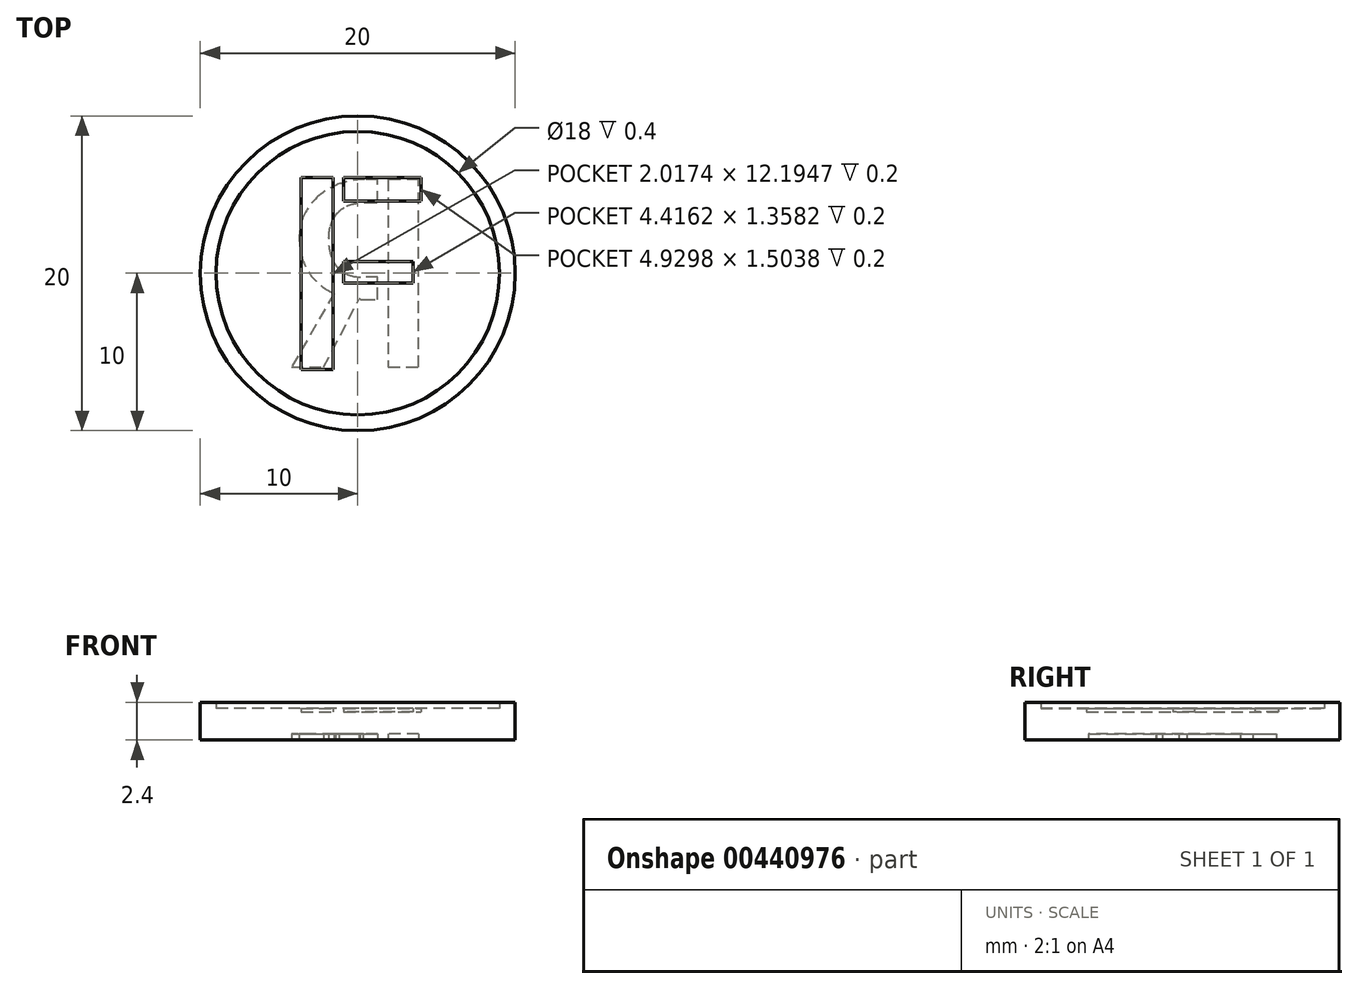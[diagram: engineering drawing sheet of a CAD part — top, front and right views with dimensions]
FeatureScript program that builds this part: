
annotation { "Feature Type Name" : "Feature", "Feature Type Description" : "" }
export const myFeature = defineFeature(function(context is Context, id is Id, definition is map)
    precondition{}
    {
        {
            var Q0;
            Q0=qCreatedBy(makeId("Top.planeOp"),FACE);
            var sketch = newSketch(context, id + "F0", { "sketchPlane" : qUnion([Q0])});
            skCircle(sketch, "E0", {"center": v(0, 0) * mm, "radius": 10 * mm});
            skText(sketch, "E1", { "text": "F", "fontName": "AllertaStencil-Regular.ttf"});
            const initialGuessF0  = {"E1": [-0.00517, -0.0061, 1, 0, 0.0122]};
            skSetInitialGuess(sketch, initialGuessF0);
            skSolve(sketch);
        }
        {
            var Q0;
            Q0=qSketchRegion(id+"F0",true);
            extrude(context, id + "F1", {"entities" : qUnion([Q0]), "depth" : 2 * mm});
        }
        {
            var Q0;
            Q0=makeQuery(id+"F0.imprint","IMPRINT",FACE,{"disambiguationData":[TD([[makeQuery(id+"F0.imprint","IMPRINT",EDGE,{"derivedFrom":sQuery(id+"F0.wireOp",EDGE,"E1.sketch_text.stroke-0")}),-1.0]])]});
            var Q1;
            Q1=makeQuery(id+"F0.imprint","IMPRINT",FACE,{"disambiguationData":[TD([[makeQuery(id+"F0.imprint","IMPRINT",EDGE,{"derivedFrom":sQuery(id+"F0.wireOp",EDGE,"E1.sketch_text.stroke-8")}),-1.0]])]});
            var Q2;
            Q2=makeQuery(id+"F0.imprint","IMPRINT",FACE,{"disambiguationData":[TD([[makeQuery(id+"F0.imprint","IMPRINT",EDGE,{"derivedFrom":sQuery(id+"F0.wireOp",EDGE,"E1.sketch_text.stroke-4")}),-1.0]])]});
            extrude(context, id + "F2", {"entities" : qUnion([Q0, Q1, Q2]), "operationType" : NewBodyOperationType.ADD, "depth" : 1.8 * mm});
        }
        {
            var Q0;
            Q0=makeQuery(id+"F1.opExtrude","CAP_FACE",FACE,{"disambiguationData":[OSD([sQuery(id+"F0.wireOp",EDGE,"E0"),sQuery(id+"F0.wireOp",EDGE,"E1.sketch_text.stroke-0"),sQuery(id+"F0.wireOp",EDGE,"E1.sketch_text.stroke-1"),sQuery(id+"F0.wireOp",EDGE,"E1.sketch_text.stroke-2"),sQuery(id+"F0.wireOp",EDGE,"E1.sketch_text.stroke-3"),sQuery(id+"F0.wireOp",EDGE,"E1.sketch_text.stroke-4"),sQuery(id+"F0.wireOp",EDGE,"E1.sketch_text.stroke-5")])],"isStart":false});
            var sketch = newSketch(context, id + "F3", { "sketchPlane" : qUnion([Q0])});
            skCircle(sketch, "E2.0.0", {"center": v(0, 0) * mm, "radius": 10 * mm});
            skCircle(sketch, "E3.0", {"center": v(0, 0) * mm, "radius": 9 * mm});
            skSolve(sketch);
        }
        {
            var Q0;
            Q0=makeQuery(id+"F3.imprint","IMPRINT",FACE,{"disambiguationData":[TD([[makeQuery(id+"F3.imprint","IMPRINT",EDGE,{"derivedFrom":sQuery(id+"F3.wireOp",EDGE,"E2.0.0")}),1.0]])]});
            extrude(context, id + "F4", {"entities" : qUnion([Q0]), "operationType" : NewBodyOperationType.ADD, "depth" : .4 * mm});
        }
        {
            var Q0;
            {var subQ0=sQuery(id+"F0.wireOp",EDGE,"E1.sketch_text.stroke-5");var subQ1=sQuery(id+"F0.wireOp",EDGE,"E1.sketch_text.stroke-4");var subQ2=sQuery(id+"F0.wireOp",EDGE,"E1.sketch_text.stroke-3");var subQ3=sQuery(id+"F0.wireOp",EDGE,"E1.sketch_text.stroke-2");var subQ4=sQuery(id+"F0.wireOp",EDGE,"E1.sketch_text.stroke-1");var subQ5=sQuery(id+"F0.wireOp",EDGE,"E1.sketch_text.stroke-0");Q0=makeQuery(id+"F2.boolean.opBoolean","MERGE",FACE,{"derivedFrom":[makeQuery(id+"F1.opExtrude","CAP_FACE",FACE,{"disambiguationData":[OSD([sQuery(id+"F0.wireOp",EDGE,"E0"),subQ5,subQ4,subQ3,subQ2,subQ1,subQ0])],"isStart":true}),makeQuery(id+"F2.opExtrude","CAP_FACE",FACE,{"disambiguationData":[OSD([subQ5,subQ4,subQ3,subQ2,subQ1,subQ0])],"isStart":true})]});}
            var sketch = newSketch(context, id + "F5", { "sketchPlane" : qUnion([Q0])});
            skCircle(sketch, "E4.0", {"center": v(0, 0) * mm, "radius": 9 * mm});
            skText(sketch, "E5", { "text": "R", "fontName": "AllertaStencil-Regular.ttf"});
            const initialGuessF5  = {"E5": [0.00533, 0.00597, -1, 0, 0.01193]};
            skSetInitialGuess(sketch, initialGuessF5);
            skSolve(sketch);
        }
        {
            var Q0;
            Q0=makeQuery(id+"F5.imprint","IMPRINT",FACE,{"disambiguationData":[TD([[makeQuery(id+"F5.imprint","IMPRINT",EDGE,{"derivedFrom":sQuery(id+"F5.wireOp",EDGE,"E5.sketch_text.stroke-0")}),-1.0]])]});
            var Q1;
            Q1=makeQuery(id+"F5.imprint","IMPRINT",FACE,{"disambiguationData":[TD([[makeQuery(id+"F5.imprint","IMPRINT",EDGE,{"derivedFrom":sQuery(id+"F5.wireOp",EDGE,"E5.sketch_text.stroke-4")}),-1.0]])]});
            extrude(context, id + "F6", {"entities" : qUnion([Q0, Q1]), "operationType" : NewBodyOperationType.REMOVE, "oppositeDirection" : true, "depth" : .4 * mm});
        }
        {
            var Q0;
            Q0=makeQuery(id+"F2.opExtrude","CAP_FACE",FACE,{"disambiguationData":[OSD([sQuery(id+"F0.wireOp",EDGE,"E1.sketch_text.stroke-0"),sQuery(id+"F0.wireOp",EDGE,"E1.sketch_text.stroke-1"),sQuery(id+"F0.wireOp",EDGE,"E1.sketch_text.stroke-2"),sQuery(id+"F0.wireOp",EDGE,"E1.sketch_text.stroke-3"),sQuery(id+"F0.wireOp",EDGE,"E1.sketch_text.stroke-4"),sQuery(id+"F0.wireOp",EDGE,"E1.sketch_text.stroke-5")])],"isStart":false});
            var Q1;
            Q1=makeQuery(id+"F2.opExtrude","CAP_FACE",FACE,{"disambiguationData":[OSD([sQuery(id+"F0.wireOp",EDGE,"E1.sketch_text.stroke-8"),sQuery(id+"F0.wireOp",EDGE,"E1.sketch_text.stroke-9"),sQuery(id+"F0.wireOp",EDGE,"E1.sketch_text.stroke-10"),sQuery(id+"F0.wireOp",EDGE,"E1.sketch_text.stroke-11")])],"isStart":false});
            var Q2;
            Q2=makeQuery(id+"F2.opExtrude","CAP_FACE",FACE,{"disambiguationData":[OSD([sQuery(id+"F0.wireOp",EDGE,"E1.sketch_text.stroke-4"),sQuery(id+"F0.wireOp",EDGE,"E1.sketch_text.stroke-5"),sQuery(id+"F0.wireOp",EDGE,"E1.sketch_text.stroke-6"),sQuery(id+"F0.wireOp",EDGE,"E1.sketch_text.stroke-7")])],"isStart":false});
            extrude(context, id + "F7", {"entities" : qUnion([Q0, Q1, Q2]), "depth" : .2 * mm});
        }
    });
